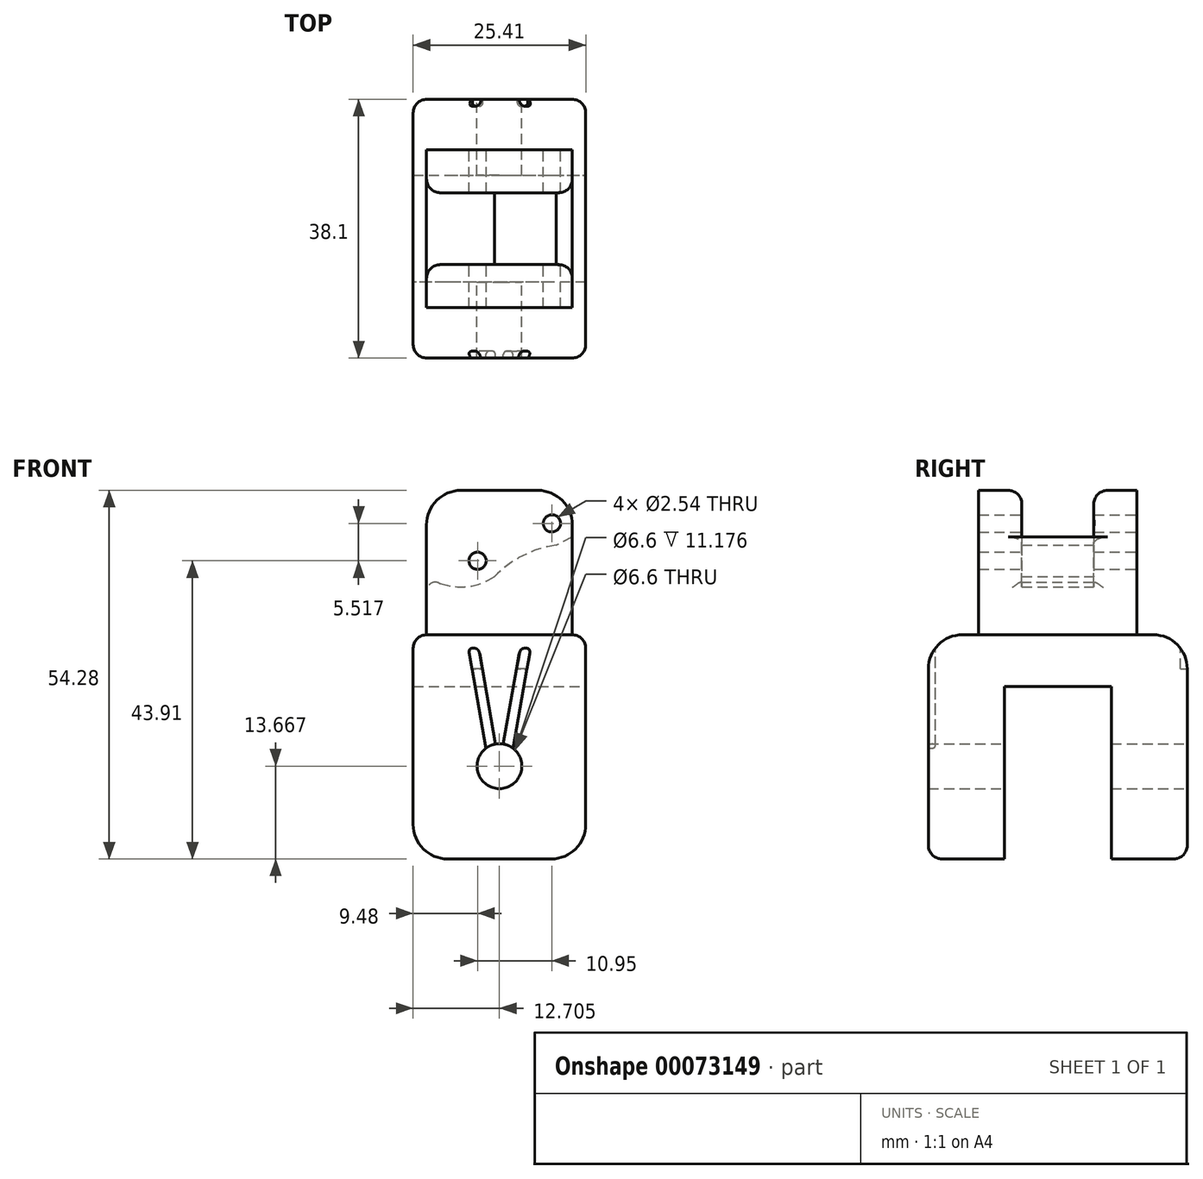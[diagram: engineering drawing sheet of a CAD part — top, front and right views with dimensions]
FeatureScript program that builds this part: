
annotation { "Feature Type Name" : "Feature", "Feature Type Description" : "" }
export const myFeature = defineFeature(function(context is Context, id is Id, definition is map)
    precondition{}
    {
        {
            var Q0;
            Q0=qCreatedBy(makeId("Front.planeOp"),FACE);
            var sketch = newSketch(context, id + "F0", { "sketchPlane" : qUnion([Q0])});
            skLineSegment(sketch, "E0.rect.bottom", {"start": v(5, -4.28) * mm, "end": v(-5, -4.28) * mm});
            skLineSegment(sketch, "E0.rect.left", {"start": v(5, -4.28) * mm, "end": v(5, 4.28) * mm});
            skLineSegment(sketch, "E0.rect.right", {"start": v(-5, -4.28) * mm, "end": v(-5, 4.28) * mm});
            skPoint(sketch, "E0.rect.middle", {"position": v(0, 0) * mm});
            skArc(sketch, "E1", {"start": v(-5, 4.28) * mm, "mid": v(0, 2.77) * mm, "end": v(5, 4.28) * mm});
            skLineSegment(sketch, "E2", {"start": v(16.45, 10.13) * mm, "end": v(16.45, -4.28) * mm});
            skLineSegment(sketch, "E3", {"start": v(16.45, -4.28) * mm, "end": v(5, -4.28) * mm});
            skLineSegment(sketch, "E4", {"start": v(5, 4.28) * mm, "end": v(16.45, 10.13) * mm});
            skArc(sketch, "E5", {"start": v(14.09, 8.92) * mm, "mid": v(9.16, 7.36) * mm, "end": v(5, 4.28) * mm});
            skSolve(sketch);
        }
        {
            var Q0;
            Q0=makeQuery(id+"F0.imprint","IMPRINT",FACE,{"disambiguationData":[TD([[makeQuery(id+"F0.imprint","IMPRINT",EDGE,{"derivedFrom":sQuery(id+"F0.wireOp",EDGE,"E0.rect.bottom")}),-1.0]])]});
            var Q1;
            Q1=makeQuery(id+"F0.imprint","IMPRINT",FACE,{"disambiguationData":[TD([[makeQuery(id+"F0.imprint","IMPRINT",EDGE,{"derivedFrom":sQuery(id+"F0.wireOp",EDGE,"E0.rect.left")}),-1.0]])]});
            var Q2;
            {var subQ0=sQuery(id+"F0.wireOp",EDGE,"E5");Q2=makeQuery(id+"F0.imprint","IMPRINT",FACE,{"disambiguationData":[TD([[makeQuery(id+"F0.imprint","IMPRINT",EDGE,{"derivedFrom":subQ0}),1.0]])]});}
            extrude(context, id + "F1", {"entities" : qUnion([Q0, Q1, Q2]), "depth" : 10.6 * mm});
        }
        {
            var Q0;
            Q0=makeQuery(id+"F1.opExtrude","SWEPT_EDGE",EDGE,{"disambiguationData":[OSD([sQuery(id+"F0.wireOp",EDGE,"E0.rect.right"),sQuery(id+"F0.wireOp",EDGE,"E1")])]});
            fillet(context, id + "F2", {"entities" : qUnion([Q0]), "radius" : 1.27 * mm, "tangentPropagation" : true, "allowEdgeOverflow" : false});
        }
        {
            var Q0;
            Q0=makeQuery(id+"F1.opExtrude","CAP_FACE",FACE,{"disambiguationData":[OSD([sQuery(id+"F0.wireOp",EDGE,"E0.rect.bottom"),sQuery(id+"F0.wireOp",EDGE,"E0.rect.top"),sQuery(id+"F0.wireOp",EDGE,"E0.rect.left"),sQuery(id+"F0.wireOp",EDGE,"E0.rect.right")])],"isStart":false});
            var sketch = newSketch(context, id + "F3", { "sketchPlane" : qUnion([Q0])});
            skLineSegment(sketch, "E6.bottom", {"start": v(-5, -4.28) * mm, "end": v(16.45, -4.28) * mm});
            skLineSegment(sketch, "E6.top", {"start": v(-5, 16.98) * mm, "end": v(16.45, 16.98) * mm});
            skLineSegment(sketch, "E6.left", {"start": v(-5, -4.28) * mm, "end": v(-5, 16.98) * mm});
            skLineSegment(sketch, "E6.right", {"start": v(16.45, -4.28) * mm, "end": v(16.45, 16.98) * mm});
            skSolve(sketch);
        }
        {
            var Q0;
            Q0=qSketchRegion(id+"F3",true);
            extrude(context, id + "F4", {"entities" : qUnion([Q0]), "operationType" : NewBodyOperationType.ADD, "depth" : 6.35 * mm});
        }
        {
            var Q0;
            Q0=makeQuery(id+"F1.opExtrude","CAP_FACE",FACE,{"disambiguationData":[OSD([sQuery(id+"F0.wireOp",EDGE,"E0.rect.bottom"),sQuery(id+"F0.wireOp",EDGE,"E0.rect.top"),sQuery(id+"F0.wireOp",EDGE,"E0.rect.left"),sQuery(id+"F0.wireOp",EDGE,"E0.rect.right")])],"isStart":true});
            var sketch = newSketch(context, id + "F5", { "sketchPlane" : qUnion([Q0])});
            skLineSegment(sketch, "E7.bottom", {"start": v(5, -4.28) * mm, "end": v(-16.45, -4.28) * mm});
            skLineSegment(sketch, "E7.top", {"start": v(5, 16.98) * mm, "end": v(-16.45, 16.98) * mm});
            skLineSegment(sketch, "E7.left", {"start": v(5, -4.28) * mm, "end": v(5, 16.98) * mm});
            skLineSegment(sketch, "E7.right", {"start": v(-16.45, -4.28) * mm, "end": v(-16.45, 16.98) * mm});
            skSolve(sketch);
        }
        {
            var Q0;
            Q0=qSketchRegion(id+"F5",true);
            extrude(context, id + "F6", {"entities" : qUnion([Q0]), "operationType" : NewBodyOperationType.ADD, "depth" : 6.35 * mm});
        }
        {
            var Q0;
            Q0=makeQuery(id+"F6.opExtrude","CAP_FACE",FACE,{"disambiguationData":[OSD([sQuery(id+"F5.wireOp",EDGE,"E7.bottom"),sQuery(id+"F5.wireOp",EDGE,"E7.top"),sQuery(id+"F5.wireOp",EDGE,"E7.left"),sQuery(id+"F5.wireOp",EDGE,"E7.right")])],"isStart":false});
            var sketch = newSketch(context, id + "F7", { "sketchPlane" : qUnion([Q0])});
            skCircle(sketch, "E8", {"center": v(-13.45, 12.13) * mm, "radius": 1.27 * mm});
            skCircle(sketch, "E9", {"center": v(-2.5, 6.61) * mm, "radius": 1.27 * mm});
            skSolve(sketch);
        }
        {
            var Q0;
            Q0=qSketchRegion(id+"F7",true);
            extrude(context, id + "F8", {"entities" : qUnion([Q0]), "operationType" : NewBodyOperationType.REMOVE, "endBound" : BoundingType.THROUGH_ALL, "oppositeDirection" : true, "depth" : 25.4 * mm});
        }
        {
            var Q0;
            Q0=makeQuery(id+"F6.boolean.opBoolean","MERGE",FACE,{"derivedFrom":[makeQuery(id+"F4.boolean.opBoolean","MERGE",FACE,{"derivedFrom":[makeQuery(id+"F1.opExtrude","SWEPT_FACE",FACE,{"disambiguationData":[OSD([sQuery(id+"F0.wireOp",EDGE,"E0.rect.bottom")])]}),makeQuery(id+"F4.opExtrude","SWEPT_FACE",FACE,{"disambiguationData":[OSD([sQuery(id+"F3.wireOp",EDGE,"E6.bottom")])]})]}),makeQuery(id+"F6.opExtrude","SWEPT_FACE",FACE,{"disambiguationData":[OSD([sQuery(id+"F5.wireOp",EDGE,"E7.bottom")])]})]});
            var sketch = newSketch(context, id + "F9", { "sketchPlane" : qUnion([Q0])});
            skLineSegment(sketch, "E10", {"start": v(16.45, -6.35) * mm, "end": v(-5, 16.95) * mm});
            skLineSegment(sketch, "E11", {"start": v(-5, -6.35) * mm, "end": v(16.45, 16.95) * mm});
            skLineSegment(sketch, "E12.rect.bottom", {"start": v(18.43, 24.35) * mm, "end": v(-6.97, 24.35) * mm});
            skLineSegment(sketch, "E12.rect.top", {"start": v(18.43, -13.75) * mm, "end": v(-6.97, -13.75) * mm});
            skLineSegment(sketch, "E12.rect.left", {"start": v(18.43, 24.35) * mm, "end": v(18.43, -13.75) * mm});
            skLineSegment(sketch, "E12.rect.right", {"start": v(-6.98, 24.35) * mm, "end": v(-6.97, -13.75) * mm});
            skPoint(sketch, "E12.rect.middle", {"position": v(5.72, 5.3) * mm});
            skSolve(sketch);
        }
        {
            var Q0;
            Q0=qSketchRegion(id+"F9",true);
            extrude(context, id + "F10", {"entities" : qUnion([Q0]), "operationType" : NewBodyOperationType.ADD, "depth" : 7.62 * mm});
        }
        {
            var Q0;
            Q0=makeQuery(id+"F10.opExtrude","CAP_FACE",FACE,{"disambiguationData":[OSD([sQuery(id+"F9.wireOp",EDGE,"E12.rect.bottom"),sQuery(id+"F9.wireOp",EDGE,"E12.rect.top"),sQuery(id+"F9.wireOp",EDGE,"E12.rect.left"),sQuery(id+"F9.wireOp",EDGE,"E12.rect.right")])],"isStart":false});
            var sketch = newSketch(context, id + "F11", { "sketchPlane" : qUnion([Q0])});
            skLineSegment(sketch, "E13.top", {"start": v(18.43, 13.17) * mm, "end": v(-6.98, 13.17) * mm});
            skLineSegment(sketch, "E14", {"start": v(-6.98, -2.57) * mm, "end": v(18.43, -2.57) * mm});
            skSolve(sketch);
        }
        {
            var Q0;
            {var subQ0=sQuery(id+"F11.wireOp",EDGE,"E14");Q0=makeQuery(id+"F11.imprint","IMPRINT",FACE,{"disambiguationData":[TD([[makeQuery(id+"F11.imprint","IMPRINT",EDGE,{"derivedFrom":subQ0}),-1.0]])]});}
            var Q1;
            {var subQ5=makeQuery(id+"F10.opExtrude","CAP_EDGE",EDGE,{"disambiguationData":[OSD([sQuery(id+"F9.wireOp",EDGE,"E12.rect.bottom")])],"isStart":false});Q1=makeQuery(id+"F11.imprint","IMPRINT",FACE,{"disambiguationData":[TD([[makeQuery(id+"F11.imprint","IMPRINT",EDGE,{"derivedFrom":subQ5}),1.0]])]});}
            extrude(context, id + "F12", {"entities" : qUnion([Q0, Q1]), "operationType" : NewBodyOperationType.ADD, "depth" : 25.4 * mm});
        }
        {
            var Q0;
            {var subQ0=sQuery(id+"F9.wireOp",EDGE,"E12.rect.top");Q0=makeQuery(id+"F12.boolean.opBoolean","MERGE",FACE,{"derivedFrom":[makeQuery(id+"F10.opExtrude","SWEPT_FACE",FACE,{"disambiguationData":[OSD([subQ0])]}),makeQuery(id+"F12.opExtrude","SWEPT_FACE",FACE,{"disambiguationData":[OSD([subQ0])]})]});}
            var sketch = newSketch(context, id + "F13", { "sketchPlane" : qUnion([Q0])});
            skCircle(sketch, "E15", {"center": v(-5.73, -23.63) * mm, "radius": 3.3 * mm});
            skSolve(sketch);
        }
        {
            var Q0;
            Q0=qSketchRegion(id+"F13",true);
            extrude(context, id + "F14", {"entities" : qUnion([Q0]), "operationType" : NewBodyOperationType.REMOVE, "endBound" : BoundingType.THROUGH_ALL, "oppositeDirection" : true, "depth" : 25.4 * mm});
        }
        {
            var Q0;
            {var subQ0=sQuery(id+"F9.wireOp",EDGE,"E12.rect.right");var subQ1=makeQuery(id+"F10.opExtrude","CAP_EDGE",EDGE,{"disambiguationData":[OSD([subQ0])],"isStart":false});Q0=makeQuery(id+"F12.opExtrude","CAP_EDGE",EDGE,{"disambiguationData":[OSD([subQ0]),TDD([makeQuery(id+"F11.imprint","IMPRINT",EDGE,{"disambiguationData":[TD([[makeQuery(id+"F11.imprint","INTERSECT",VERTEX,{"derivedFrom":[makeQuery(id+"F10.opExtrude","CAP_EDGE",EDGE,{"disambiguationData":[OSD([sQuery(id+"F9.wireOp",EDGE,"E12.rect.top")])],"isStart":false}),subQ1]}),1.0]])],"derivedFrom":subQ1})])],"isStart":false});}
            var Q1;
            {var subQ0=sQuery(id+"F9.wireOp",EDGE,"E12.rect.left");var subQ1=makeQuery(id+"F10.opExtrude","CAP_EDGE",EDGE,{"disambiguationData":[OSD([subQ0])],"isStart":false});Q1=makeQuery(id+"F12.opExtrude","CAP_EDGE",EDGE,{"disambiguationData":[OSD([subQ0]),TDD([makeQuery(id+"F11.imprint","IMPRINT",EDGE,{"disambiguationData":[TD([[makeQuery(id+"F11.imprint","INTERSECT",VERTEX,{"derivedFrom":[makeQuery(id+"F10.opExtrude","CAP_EDGE",EDGE,{"disambiguationData":[OSD([sQuery(id+"F9.wireOp",EDGE,"E12.rect.top")])],"isStart":false}),subQ1]}),1.0]])],"derivedFrom":subQ1})])],"isStart":false});}
            var Q2;
            {var subQ0=sQuery(id+"F9.wireOp",EDGE,"E12.rect.right");var subQ1=makeQuery(id+"F10.opExtrude","CAP_EDGE",EDGE,{"disambiguationData":[OSD([subQ0])],"isStart":false});Q2=makeQuery(id+"F12.opExtrude","CAP_EDGE",EDGE,{"disambiguationData":[OSD([subQ0]),TDD([makeQuery(id+"F11.imprint","IMPRINT",EDGE,{"disambiguationData":[TD([[makeQuery(id+"F11.imprint","INTERSECT",VERTEX,{"derivedFrom":[makeQuery(id+"F10.opExtrude","CAP_EDGE",EDGE,{"disambiguationData":[OSD([sQuery(id+"F9.wireOp",EDGE,"E12.rect.bottom")])],"isStart":false}),subQ1]}),-1.0]])],"derivedFrom":subQ1})])],"isStart":false});}
            var Q3;
            {var subQ0=sQuery(id+"F9.wireOp",EDGE,"E12.rect.left");var subQ1=makeQuery(id+"F10.opExtrude","CAP_EDGE",EDGE,{"disambiguationData":[OSD([subQ0])],"isStart":false});Q3=makeQuery(id+"F12.opExtrude","CAP_EDGE",EDGE,{"disambiguationData":[OSD([subQ0]),TDD([makeQuery(id+"F11.imprint","IMPRINT",EDGE,{"disambiguationData":[TD([[makeQuery(id+"F11.imprint","INTERSECT",VERTEX,{"derivedFrom":[makeQuery(id+"F10.opExtrude","CAP_EDGE",EDGE,{"disambiguationData":[OSD([sQuery(id+"F9.wireOp",EDGE,"E12.rect.bottom")])],"isStart":false}),subQ1]}),-1.0]])],"derivedFrom":subQ1})])],"isStart":false});}
            var Q4;
            Q4=makeQuery(id+"F12.opExtrude","CAP_EDGE",EDGE,{"disambiguationData":[OSD([sQuery(id+"F11.wireOp",EDGE,"E13.top")])],"isStart":true});
            var Q5;
            Q5=makeQuery(id+"F12.opExtrude","CAP_EDGE",EDGE,{"disambiguationData":[OSD([sQuery(id+"F11.wireOp",EDGE,"E14")])],"isStart":true});
            var Q6;
            Q6=makeQuery(id+"F6.boolean.opBoolean","MERGE",EDGE,{"derivedFrom":[makeQuery(id+"F4.boolean.opBoolean","MERGE",EDGE,{"derivedFrom":[makeQuery(id+"F1.opExtrude","SWEPT_EDGE",EDGE,{"disambiguationData":[OSD([sQuery(id+"F0.wireOp",EDGE,"E0.rect.bottom"),sQuery(id+"F0.wireOp",EDGE,"E0.rect.right")])]}),makeQuery(id+"F4.opExtrude","SWEPT_EDGE",EDGE,{"disambiguationData":[OSD([sQuery(id+"F3.wireOp",EDGE,"E6.bottom"),sQuery(id+"F3.wireOp",EDGE,"E6.left")])]})]}),makeQuery(id+"F6.opExtrude","SWEPT_EDGE",EDGE,{"disambiguationData":[OSD([sQuery(id+"F5.wireOp",EDGE,"E7.bottom"),sQuery(id+"F5.wireOp",EDGE,"E7.left")])]})]});
            var Q7;
            Q7=makeQuery(id+"F4.opExtrude","CAP_EDGE",EDGE,{"disambiguationData":[OSD([sQuery(id+"F3.wireOp",EDGE,"E6.bottom")])],"isStart":false});
            var Q8;
            Q8=makeQuery(id+"F6.boolean.opBoolean","MERGE",EDGE,{"derivedFrom":[makeQuery(id+"F4.boolean.opBoolean","MERGE",EDGE,{"derivedFrom":[makeQuery(id+"F1.opExtrude","SWEPT_EDGE",EDGE,{"disambiguationData":[OSD([sQuery(id+"F0.wireOp",EDGE,"E2"),sQuery(id+"F0.wireOp",EDGE,"E3")])]}),makeQuery(id+"F4.opExtrude","SWEPT_EDGE",EDGE,{"disambiguationData":[OSD([sQuery(id+"F3.wireOp",EDGE,"E6.bottom"),sQuery(id+"F3.wireOp",EDGE,"E6.right")])]})]}),makeQuery(id+"F6.opExtrude","SWEPT_EDGE",EDGE,{"disambiguationData":[OSD([sQuery(id+"F5.wireOp",EDGE,"E7.bottom"),sQuery(id+"F5.wireOp",EDGE,"E7.right")])]})]});
            var Q9;
            Q9=makeQuery(id+"F6.opExtrude","CAP_EDGE",EDGE,{"disambiguationData":[OSD([sQuery(id+"F5.wireOp",EDGE,"E7.bottom")])],"isStart":false});
            var Q10;
            Q10=makeQuery(id+"F6.opExtrude","SWEPT_EDGE",EDGE,{"disambiguationData":[OSD([sQuery(id+"F5.wireOp",EDGE,"E7.top"),sQuery(id+"F5.wireOp",EDGE,"E7.right")])]});
            var Q11;
            Q11=makeQuery(id+"F6.opExtrude","SWEPT_EDGE",EDGE,{"disambiguationData":[OSD([sQuery(id+"F5.wireOp",EDGE,"E7.top"),sQuery(id+"F5.wireOp",EDGE,"E7.left")])]});
            var Q12;
            Q12=makeQuery(id+"F4.opExtrude","SWEPT_EDGE",EDGE,{"disambiguationData":[OSD([sQuery(id+"F3.wireOp",EDGE,"E6.top"),sQuery(id+"F3.wireOp",EDGE,"E6.right")])]});
            var Q13;
            Q13=makeQuery(id+"F4.opExtrude","SWEPT_EDGE",EDGE,{"disambiguationData":[OSD([sQuery(id+"F3.wireOp",EDGE,"E6.top"),sQuery(id+"F3.wireOp",EDGE,"E6.left")])]});
            fillet(context, id + "F15", {"entities" : qUnion([Q0, Q1, Q2, Q3, Q4, Q5, Q6, Q7, Q8, Q9, Q10, Q11, Q12, Q13]), "radius" : 5.08 * mm, "tangentPropagation" : true, "allowEdgeOverflow" : false});
        }
        {
            var Q0;
            Q0=makeQuery(id+"F10.opExtrude","CAP_EDGE",EDGE,{"disambiguationData":[OSD([sQuery(id+"F9.wireOp",EDGE,"E12.rect.top")])],"isStart":true});
            var Q1;
            Q1=makeQuery(id+"F10.opExtrude","CAP_EDGE",EDGE,{"disambiguationData":[OSD([sQuery(id+"F9.wireOp",EDGE,"E12.rect.bottom")])],"isStart":true});
            var Q2;
            {var subQ0=sQuery(id+"F9.wireOp",EDGE,"E12.rect.right");var subQ1=makeQuery(id+"F10.opExtrude","CAP_EDGE",EDGE,{"disambiguationData":[OSD([subQ0])],"isStart":false});Q2=makeQuery(id+"F15.opFillet","BLEND_EDGE",EDGE,{"blendedFrom":[makeQuery(id+"F6.boolean.opBoolean","MERGE",EDGE,{"derivedFrom":[makeQuery(id+"F4.boolean.opBoolean","MERGE",EDGE,{"derivedFrom":[makeQuery(id+"F1.opExtrude","SWEPT_EDGE",EDGE,{"disambiguationData":[OSD([sQuery(id+"F0.wireOp",EDGE,"E0.rect.bottom"),sQuery(id+"F0.wireOp",EDGE,"E0.rect.right")])]}),makeQuery(id+"F4.opExtrude","SWEPT_EDGE",EDGE,{"disambiguationData":[OSD([sQuery(id+"F3.wireOp",EDGE,"E6.bottom"),sQuery(id+"F3.wireOp",EDGE,"E6.left")])]})]}),makeQuery(id+"F6.opExtrude","SWEPT_EDGE",EDGE,{"disambiguationData":[OSD([sQuery(id+"F5.wireOp",EDGE,"E7.bottom"),sQuery(id+"F5.wireOp",EDGE,"E7.left")])]})]}),makeQuery(id+"F12.boolean.opBoolean","MERGE",FACE,{"derivedFrom":[makeQuery(id+"F10.opExtrude","SWEPT_FACE",FACE,{"disambiguationData":[OSD([subQ0])]}),makeQuery(id+"F12.opExtrude","SWEPT_FACE",FACE,{"disambiguationData":[OSD([subQ0]),TDD([makeQuery(id+"F11.imprint","IMPRINT",EDGE,{"disambiguationData":[TD([[makeQuery(id+"F11.imprint","INTERSECT",VERTEX,{"derivedFrom":[makeQuery(id+"F10.opExtrude","CAP_EDGE",EDGE,{"disambiguationData":[OSD([sQuery(id+"F9.wireOp",EDGE,"E12.rect.bottom")])],"isStart":false}),subQ1]}),-1.0]])],"derivedFrom":subQ1})])]}),makeQuery(id+"F12.opExtrude","SWEPT_FACE",FACE,{"disambiguationData":[OSD([subQ0]),TDD([makeQuery(id+"F11.imprint","IMPRINT",EDGE,{"disambiguationData":[TD([[makeQuery(id+"F11.imprint","INTERSECT",VERTEX,{"derivedFrom":[makeQuery(id+"F10.opExtrude","CAP_EDGE",EDGE,{"disambiguationData":[OSD([sQuery(id+"F9.wireOp",EDGE,"E12.rect.top")])],"isStart":false}),subQ1]}),1.0]])],"derivedFrom":subQ1})])]})]})],"blendedInto":[makeQuery(id+"F12.boolean.opBoolean","MERGE",FACE,{"derivedFrom":[makeQuery(id+"F10.opExtrude","SWEPT_FACE",FACE,{"disambiguationData":[OSD([subQ0])]}),makeQuery(id+"F12.opExtrude","SWEPT_FACE",FACE,{"disambiguationData":[OSD([subQ0]),TDD([makeQuery(id+"F11.imprint","IMPRINT",EDGE,{"disambiguationData":[TD([[makeQuery(id+"F11.imprint","INTERSECT",VERTEX,{"derivedFrom":[makeQuery(id+"F10.opExtrude","CAP_EDGE",EDGE,{"disambiguationData":[OSD([sQuery(id+"F9.wireOp",EDGE,"E12.rect.bottom")])],"isStart":false}),subQ1]}),-1.0]])],"derivedFrom":subQ1})])]}),makeQuery(id+"F12.opExtrude","SWEPT_FACE",FACE,{"disambiguationData":[OSD([subQ0]),TDD([makeQuery(id+"F11.imprint","IMPRINT",EDGE,{"disambiguationData":[TD([[makeQuery(id+"F11.imprint","INTERSECT",VERTEX,{"derivedFrom":[makeQuery(id+"F10.opExtrude","CAP_EDGE",EDGE,{"disambiguationData":[OSD([sQuery(id+"F9.wireOp",EDGE,"E12.rect.top")])],"isStart":false}),subQ1]}),1.0]])],"derivedFrom":subQ1})])]})]})]});}
            var Q3;
            {var subQ0=sQuery(id+"F9.wireOp",EDGE,"E12.rect.left");var subQ1=makeQuery(id+"F10.opExtrude","CAP_EDGE",EDGE,{"disambiguationData":[OSD([subQ0])],"isStart":false});Q3=makeQuery(id+"F15.opFillet","BLEND_EDGE",EDGE,{"blendedFrom":[makeQuery(id+"F6.boolean.opBoolean","MERGE",EDGE,{"derivedFrom":[makeQuery(id+"F4.boolean.opBoolean","MERGE",EDGE,{"derivedFrom":[makeQuery(id+"F1.opExtrude","SWEPT_EDGE",EDGE,{"disambiguationData":[OSD([sQuery(id+"F0.wireOp",EDGE,"E2"),sQuery(id+"F0.wireOp",EDGE,"E3")])]}),makeQuery(id+"F4.opExtrude","SWEPT_EDGE",EDGE,{"disambiguationData":[OSD([sQuery(id+"F3.wireOp",EDGE,"E6.bottom"),sQuery(id+"F3.wireOp",EDGE,"E6.right")])]})]}),makeQuery(id+"F6.opExtrude","SWEPT_EDGE",EDGE,{"disambiguationData":[OSD([sQuery(id+"F5.wireOp",EDGE,"E7.bottom"),sQuery(id+"F5.wireOp",EDGE,"E7.right")])]})]}),makeQuery(id+"F12.boolean.opBoolean","MERGE",FACE,{"derivedFrom":[makeQuery(id+"F10.opExtrude","SWEPT_FACE",FACE,{"disambiguationData":[OSD([subQ0])]}),makeQuery(id+"F12.opExtrude","SWEPT_FACE",FACE,{"disambiguationData":[OSD([subQ0]),TDD([makeQuery(id+"F11.imprint","IMPRINT",EDGE,{"disambiguationData":[TD([[makeQuery(id+"F11.imprint","INTERSECT",VERTEX,{"derivedFrom":[makeQuery(id+"F10.opExtrude","CAP_EDGE",EDGE,{"disambiguationData":[OSD([sQuery(id+"F9.wireOp",EDGE,"E12.rect.bottom")])],"isStart":false}),subQ1]}),-1.0]])],"derivedFrom":subQ1})])]}),makeQuery(id+"F12.opExtrude","SWEPT_FACE",FACE,{"disambiguationData":[OSD([subQ0]),TDD([makeQuery(id+"F11.imprint","IMPRINT",EDGE,{"disambiguationData":[TD([[makeQuery(id+"F11.imprint","INTERSECT",VERTEX,{"derivedFrom":[makeQuery(id+"F10.opExtrude","CAP_EDGE",EDGE,{"disambiguationData":[OSD([sQuery(id+"F9.wireOp",EDGE,"E12.rect.top")])],"isStart":false}),subQ1]}),1.0]])],"derivedFrom":subQ1})])]})]})],"blendedInto":[makeQuery(id+"F12.boolean.opBoolean","MERGE",FACE,{"derivedFrom":[makeQuery(id+"F10.opExtrude","SWEPT_FACE",FACE,{"disambiguationData":[OSD([subQ0])]}),makeQuery(id+"F12.opExtrude","SWEPT_FACE",FACE,{"disambiguationData":[OSD([subQ0]),TDD([makeQuery(id+"F11.imprint","IMPRINT",EDGE,{"disambiguationData":[TD([[makeQuery(id+"F11.imprint","INTERSECT",VERTEX,{"derivedFrom":[makeQuery(id+"F10.opExtrude","CAP_EDGE",EDGE,{"disambiguationData":[OSD([sQuery(id+"F9.wireOp",EDGE,"E12.rect.bottom")])],"isStart":false}),subQ1]}),-1.0]])],"derivedFrom":subQ1})])]}),makeQuery(id+"F12.opExtrude","SWEPT_FACE",FACE,{"disambiguationData":[OSD([subQ0]),TDD([makeQuery(id+"F11.imprint","IMPRINT",EDGE,{"disambiguationData":[TD([[makeQuery(id+"F11.imprint","INTERSECT",VERTEX,{"derivedFrom":[makeQuery(id+"F10.opExtrude","CAP_EDGE",EDGE,{"disambiguationData":[OSD([sQuery(id+"F9.wireOp",EDGE,"E12.rect.top")])],"isStart":false}),subQ1]}),1.0]])],"derivedFrom":subQ1})])]})]})]});}
            fillet(context, id + "F16", {"entities" : qUnion([Q0, Q1, Q2, Q3]), "radius" : 5 * mm, "tangentPropagation" : true, "allowEdgeOverflow" : false});
        }
        {
            var Q0;
            {var subQ0=sQuery(id+"F9.wireOp",EDGE,"E12.rect.right");var subQ1=sQuery(id+"F9.wireOp",EDGE,"E12.rect.bottom");Q0=makeQuery(id+"F12.boolean.opBoolean","MERGE",EDGE,{"derivedFrom":[makeQuery(id+"F10.opExtrude","SWEPT_EDGE",EDGE,{"disambiguationData":[OSD([subQ1,subQ0])]}),makeQuery(id+"F12.opExtrude","SWEPT_EDGE",EDGE,{"disambiguationData":[OSD([subQ1,subQ0])]})]});}
            var Q1;
            {var subQ0=sQuery(id+"F9.wireOp",EDGE,"E12.rect.right");var subQ1=sQuery(id+"F9.wireOp",EDGE,"E12.rect.top");Q1=makeQuery(id+"F12.boolean.opBoolean","MERGE",EDGE,{"derivedFrom":[makeQuery(id+"F10.opExtrude","SWEPT_EDGE",EDGE,{"disambiguationData":[OSD([subQ1,subQ0])]}),makeQuery(id+"F12.opExtrude","SWEPT_EDGE",EDGE,{"disambiguationData":[OSD([subQ1,subQ0])]})]});}
            var Q2;
            Q2=makeQuery(id+"F6.opExtrude","CAP_EDGE",EDGE,{"disambiguationData":[OSD([sQuery(id+"F5.wireOp",EDGE,"E7.top")])],"isStart":true});
            var Q3;
            Q3=makeQuery(id+"F4.opExtrude","CAP_EDGE",EDGE,{"disambiguationData":[OSD([sQuery(id+"F3.wireOp",EDGE,"E6.top")])],"isStart":true});
            fillet(context, id + "F17", {"entities" : qUnion([Q0, Q1, Q2, Q3]), "radius" : 2 * mm, "tangentPropagation" : true, "allowEdgeOverflow" : false});
        }
        {
            var Q0;
            {var subQ0=sQuery(id+"F9.wireOp",EDGE,"E12.rect.bottom");Q0=makeQuery(id+"F12.boolean.opBoolean","MERGE",FACE,{"derivedFrom":[makeQuery(id+"F10.opExtrude","SWEPT_FACE",FACE,{"disambiguationData":[OSD([subQ0])]}),makeQuery(id+"F12.opExtrude","SWEPT_FACE",FACE,{"disambiguationData":[OSD([subQ0])]})]});}
            var sketch = newSketch(context, id + "F18", { "sketchPlane" : qUnion([Q0])});
            skLineSegment(sketch, "E16", {"start": v(5.73, -23.63) * mm, "end": v(5.73, -8.92) * mm});
            skLineSegment(sketch, "E17", {"start": v(8.32, -8.92) * mm, "end": v(5.73, -23.63) * mm});
            skLineSegment(sketch, "E18", {"start": v(5.73, -23.63) * mm, "end": v(3.13, -8.92) * mm});
            skLineSegment(sketch, "E19", {"start": v(1.6, -8.92) * mm, "end": v(4.19, -23.56) * mm});
            skLineSegment(sketch, "E20", {"start": v(4.19, -23.56) * mm, "end": v(5.73, -23.63) * mm});
            skLineSegment(sketch, "E21", {"start": v(9.84, -8.92) * mm, "end": v(7.25, -23.63) * mm});
            skLineSegment(sketch, "E22", {"start": v(7.25, -23.63) * mm, "end": v(5.73, -23.63) * mm});
            skLineSegment(sketch, "E23", {"start": v(1.6, -8.92) * mm, "end": v(0.78, -4.21) * mm});
            skLineSegment(sketch, "E24", {"start": v(3.13, -8.92) * mm, "end": v(2.3, -4.21) * mm});
            skLineSegment(sketch, "E25", {"start": v(2.3, -4.21) * mm, "end": v(0.78, -4.21) * mm});
            skLineSegment(sketch, "E26", {"start": v(8.32, -8.92) * mm, "end": v(9.15, -4.21) * mm});
            skLineSegment(sketch, "E27", {"start": v(9.84, -8.92) * mm, "end": v(10.67, -4.21) * mm});
            skLineSegment(sketch, "E28", {"start": v(10.67, -4.21) * mm, "end": v(9.15, -4.21) * mm});
            skSolve(sketch);
        }
        {
            var Q0;
            {var subQ0=sQuery(id+"F9.wireOp",EDGE,"E12.rect.top");Q0=makeQuery(id+"F12.boolean.opBoolean","MERGE",FACE,{"derivedFrom":[makeQuery(id+"F10.opExtrude","SWEPT_FACE",FACE,{"disambiguationData":[OSD([subQ0])]}),makeQuery(id+"F12.opExtrude","SWEPT_FACE",FACE,{"disambiguationData":[OSD([subQ0])]})]});}
            var sketch = newSketch(context, id + "F19", { "sketchPlane" : qUnion([Q0])});
            skLineSegment(sketch, "E29", {"start": v(-5.82, -23.69) * mm, "end": v(-5.82, -8.98) * mm});
            skLineSegment(sketch, "E30", {"start": v(-3.23, -8.98) * mm, "end": v(-5.82, -23.69) * mm});
            skLineSegment(sketch, "E31", {"start": v(-5.82, -23.69) * mm, "end": v(-8.42, -8.98) * mm});
            skLineSegment(sketch, "E32", {"start": v(-9.94, -8.98) * mm, "end": v(-7.36, -23.62) * mm});
            skLineSegment(sketch, "E33", {"start": v(-7.36, -23.62) * mm, "end": v(-5.82, -23.69) * mm});
            skLineSegment(sketch, "E34", {"start": v(-1.7, -8.98) * mm, "end": v(-4.3, -23.69) * mm});
            skLineSegment(sketch, "E35", {"start": v(-4.3, -23.69) * mm, "end": v(-5.82, -23.69) * mm});
            skLineSegment(sketch, "E36", {"start": v(-9.94, -8.98) * mm, "end": v(-10.77, -4.27) * mm});
            skLineSegment(sketch, "E37", {"start": v(-8.42, -8.98) * mm, "end": v(-9.25, -4.27) * mm});
            skLineSegment(sketch, "E38", {"start": v(-9.25, -4.27) * mm, "end": v(-10.77, -4.27) * mm});
            skLineSegment(sketch, "E39", {"start": v(-3.23, -8.98) * mm, "end": v(-2.4, -4.27) * mm});
            skLineSegment(sketch, "E40", {"start": v(-1.7, -8.98) * mm, "end": v(-0.88, -4.27) * mm});
            skLineSegment(sketch, "E41", {"start": v(-0.88, -4.27) * mm, "end": v(-2.4, -4.27) * mm});
            skSolve(sketch);
        }
        {
            var Q0;
            Q0 = qSketchRegion(id + "F18", true);
            extrude(context, id + "F20", {"entities" : qUnion([Q0]), "operationType" : NewBodyOperationType.REMOVE, "oppositeDirection" : true, "depth" : 1 * mm});
        }
        {
            var Q0;
            {var subQ0=sQuery(id+"F19.wireOp",EDGE,"E38");Q0=makeQuery(id+"F19.imprint","IMPRINT",FACE,{"disambiguationData":[TD([[makeQuery(id+"F19.imprint","IMPRINT",EDGE,{"derivedFrom":subQ0}),1.0]])]});}
            var Q1;
            {var subQ0=sQuery(id+"F19.wireOp",EDGE,"E41");Q1=makeQuery(id+"F19.imprint","IMPRINT",FACE,{"disambiguationData":[TD([[makeQuery(id+"F19.imprint","IMPRINT",EDGE,{"derivedFrom":subQ0}),1.0]])]});}
            var Q2;
            {var subQ8=sQuery(id+"F19.wireOp",EDGE,"E37");var subQ9=sQuery(id+"F19.wireOp",EDGE,"E31");var subQ10=makeQuery(id+"F19.imprint","INTERSECT",VERTEX,{"derivedFrom":[subQ9,subQ8]});Q2=makeQuery(id+"F19.imprint","IMPRINT",FACE,{"disambiguationData":[TD([[makeQuery(id+"F19.imprint","IMPRINT",EDGE,{"disambiguationData":[TD([[subQ10,1.0]])],"derivedFrom":subQ9}),1.0]])]});}
            var Q3;
            {var subQ6=sQuery(id+"F19.wireOp",EDGE,"E30");var subQ10=sQuery(id+"F19.wireOp",EDGE,"E39");var subQ11=makeQuery(id+"F19.imprint","INTERSECT",VERTEX,{"derivedFrom":[subQ6,subQ10]});Q3=makeQuery(id+"F19.imprint","IMPRINT",FACE,{"disambiguationData":[TD([[makeQuery(id+"F19.imprint","IMPRINT",EDGE,{"disambiguationData":[TD([[subQ11,-1.0]])],"derivedFrom":subQ6}),1.0]])]});}
            extrude(context, id + "F21", {"entities" : qUnion([Q0, Q1, Q2, Q3]), "operationType" : NewBodyOperationType.REMOVE, "oppositeDirection" : true, "depth" : 1 * mm});
        }
        {
            var Q0;
            Q0=makeQuery(id+"F20.boolean.opBoolean","COPY",EDGE,{"derivedFrom":makeQuery(id+"F20.opExtrude","CAP_EDGE",EDGE,{"disambiguationData":[OSD([sQuery(id+"F18.wireOp",EDGE,"E18"),sQuery(id+"F18.wireOp",EDGE,"E24")])],"isStart":false})});
            var Q1;
            Q1=makeQuery(id+"F20.boolean.opBoolean","COPY",EDGE,{"derivedFrom":makeQuery(id+"F20.opExtrude","CAP_EDGE",EDGE,{"disambiguationData":[OSD([sQuery(id+"F18.wireOp",EDGE,"E19"),sQuery(id+"F18.wireOp",EDGE,"E23")])],"isStart":false})});
            var Q2;
            Q2=makeQuery(id+"F20.boolean.opBoolean","COPY",EDGE,{"derivedFrom":makeQuery(id+"F20.opExtrude","CAP_EDGE",EDGE,{"disambiguationData":[OSD([sQuery(id+"F18.wireOp",EDGE,"E21"),sQuery(id+"F18.wireOp",EDGE,"E27")])],"isStart":false})});
            var Q3;
            Q3=makeQuery(id+"F20.boolean.opBoolean","COPY",EDGE,{"derivedFrom":makeQuery(id+"F20.opExtrude","CAP_EDGE",EDGE,{"disambiguationData":[OSD([sQuery(id+"F18.wireOp",EDGE,"E17"),sQuery(id+"F18.wireOp",EDGE,"E26")])],"isStart":false})});
            var Q4;
            Q4=makeQuery(id+"F21.boolean.opBoolean","COPY",EDGE,{"derivedFrom":makeQuery(id+"F21.opExtrude","CAP_EDGE",EDGE,{"disambiguationData":[OSD([sQuery(id+"F19.wireOp",EDGE,"E32"),sQuery(id+"F19.wireOp",EDGE,"E36")])],"isStart":false})});
            var Q5;
            Q5=makeQuery(id+"F21.boolean.opBoolean","COPY",EDGE,{"derivedFrom":makeQuery(id+"F21.opExtrude","CAP_EDGE",EDGE,{"disambiguationData":[OSD([sQuery(id+"F19.wireOp",EDGE,"E31"),sQuery(id+"F19.wireOp",EDGE,"E37")])],"isStart":false})});
            var Q6;
            Q6=makeQuery(id+"F21.boolean.opBoolean","COPY",EDGE,{"derivedFrom":makeQuery(id+"F21.opExtrude","CAP_EDGE",EDGE,{"disambiguationData":[OSD([sQuery(id+"F19.wireOp",EDGE,"E34"),sQuery(id+"F19.wireOp",EDGE,"E40")])],"isStart":false})});
            var Q7;
            Q7=makeQuery(id+"F21.boolean.opBoolean","COPY",EDGE,{"derivedFrom":makeQuery(id+"F21.opExtrude","CAP_EDGE",EDGE,{"disambiguationData":[OSD([sQuery(id+"F19.wireOp",EDGE,"E30"),sQuery(id+"F19.wireOp",EDGE,"E39")])],"isStart":false})});
            fillet(context, id + "F22", {"entities" : qUnion([Q0, Q1, Q2, Q3, Q4, Q5, Q6, Q7]), "radius" : .5 * mm, "tangentPropagation" : true, "allowEdgeOverflow" : false});
        }
    });
